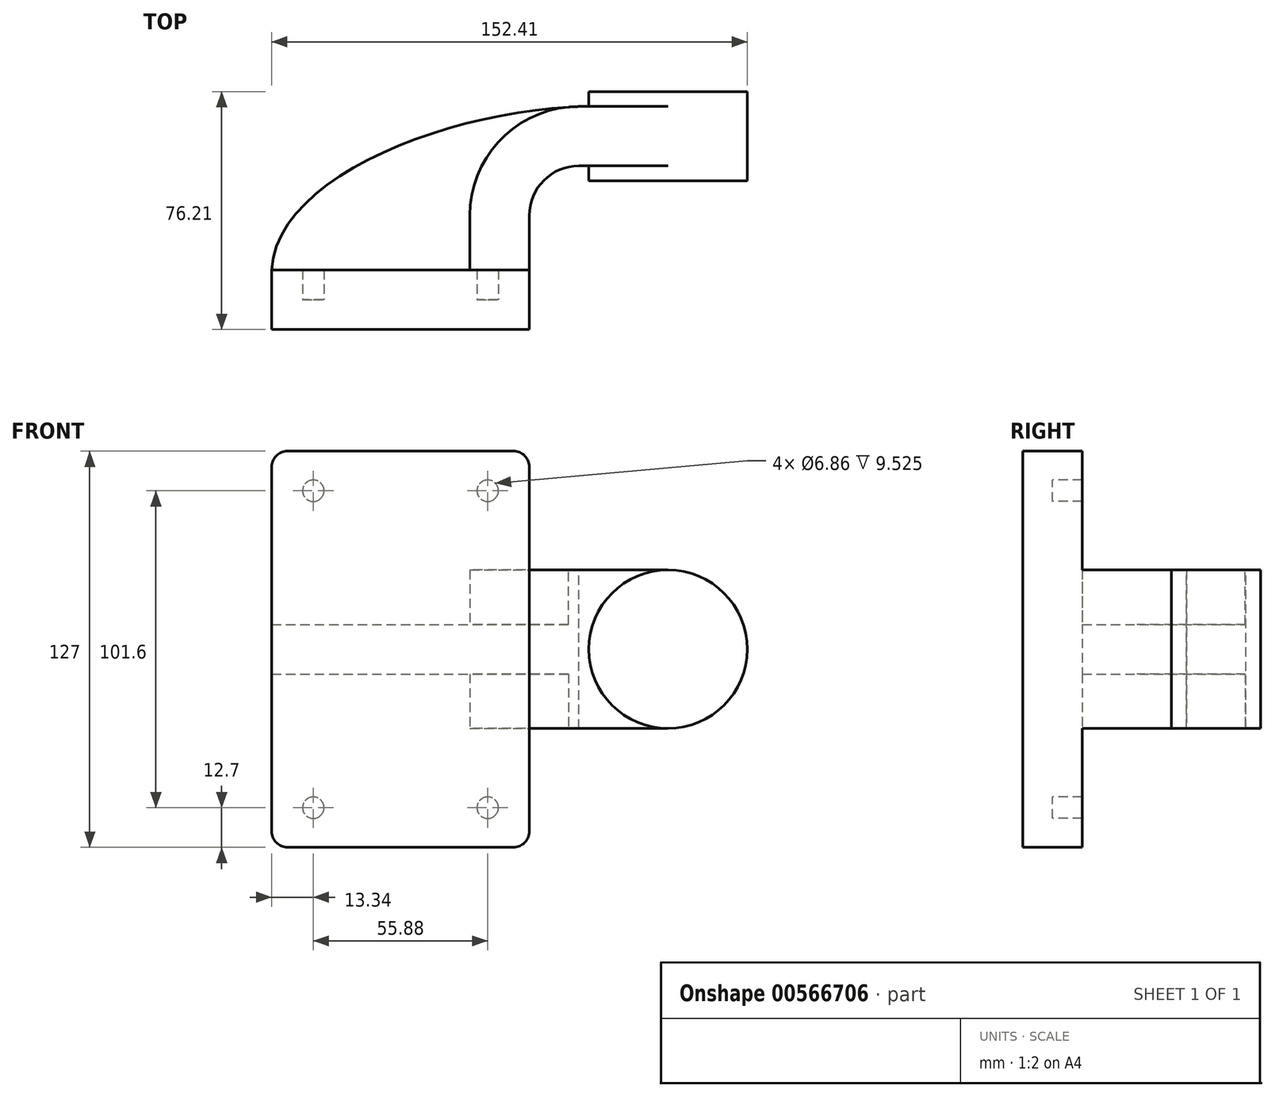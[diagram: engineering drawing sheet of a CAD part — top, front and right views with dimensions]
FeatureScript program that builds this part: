
annotation { "Feature Type Name" : "Feature", "Feature Type Description" : "" }
export const myFeature = defineFeature(function(context is Context, id is Id, definition is map)
    precondition{}
    {
        {
            var Q0;
            Q0=qCreatedBy(makeId("Top.planeOp"),FACE);
            var sketch = newSketch(context, id + "F0", { "sketchPlane" : qUnion([Q0])});
            skLineSegment(sketch, "E0.rect.bottom", {"start": v(-41.28, 9.52) * mm, "end": v(41.28, 9.52) * mm});
            skLineSegment(sketch, "E0.rect.top", {"start": v(-41.28, -9.52) * mm, "end": v(41.28, -9.52) * mm});
            skLineSegment(sketch, "E0.rect.left", {"start": v(-41.28, 9.52) * mm, "end": v(-41.28, -9.52) * mm});
            skLineSegment(sketch, "E0.rect.right", {"start": v(41.28, 9.52) * mm, "end": v(41.28, -9.52) * mm});
            skPoint(sketch, "E0.rect.middle", {"position": v(0, 0) * mm});
            skLineSegment(sketch, "E1", {"start": v(41.28, 9.52) * mm, "end": v(41.28, 27) * mm});
            skArc(sketch, "E2", {"start": v(41.28, 27) * mm, "mid": v(45.92, 38.23) * mm, "end": v(57.15, 42.88) * mm});
            skLineSegment(sketch, "E3", {"start": v(57.15, 42.88) * mm, "end": v(85.72, 42.88) * mm});
            skLineSegment(sketch, "E4.rect.bottom", {"start": v(60.32, 38.1) * mm, "end": v(111.12, 38.1) * mm});
            skLineSegment(sketch, "E4.rect.top", {"start": v(60.32, 66.68) * mm, "end": v(111.12, 66.68) * mm});
            skLineSegment(sketch, "E4.rect.left", {"start": v(60.32, 38.1) * mm, "end": v(60.32, 66.68) * mm});
            skLineSegment(sketch, "E4.rect.right", {"start": v(111.13, 38.1) * mm, "end": v(111.12, 66.68) * mm});
            skPoint(sketch, "E4.rect.middle", {"position": v(85.72, 52.39) * mm});
            skLineSegment(sketch, "E5.0", {"start": v(57.15, 61.93) * mm, "end": v(85.72, 61.93) * mm});
            skArc(sketch, "E5.1", {"start": v(22.23, 27) * mm, "mid": v(32.45, 51.7) * mm, "end": v(57.15, 61.93) * mm});
            skLineSegment(sketch, "E5.2", {"start": v(22.23, 9.52) * mm, "end": v(22.23, 27) * mm});
            skLineSegment(sketch, "E6", {"start": v(85.72, 38.1) * mm, "end": v(85.72, 66.68) * mm});
            skFitSpline(sketch, "E7", {"points": [v(-41.28, 9.53) * mm, v(57.15, 61.93) * mm], "startDerivative": vector(5.2, 92.34) * mm, "endDerivative": vector(120.92, 4.22) * mm});
            skSolve(sketch);
        }
        {
            var Q0;
            Q0=makeQuery(id+"F0.imprint","IMPRINT",FACE,{"disambiguationData":[TD([[makeQuery(id+"F0.imprint","IMPRINT",EDGE,{"derivedFrom":sQuery(id+"F0.wireOp",EDGE,"E0.rect.top")}),1.0]])]});
            extrude(context, id + "F1", {"entities" : qUnion([Q0]), "endBound" : BoundingType.SYMMETRIC, "depth" : 127 * mm, "offsetDistance" : 25.4 * mm});
        }
        {
            var Q0;
            {var subQ9=sQuery(id+"F0.wireOp",EDGE,"E1");Q0=makeQuery(id+"F0.imprint","IMPRINT",FACE,{"disambiguationData":[TD([[makeQuery(id+"F0.imprint","IMPRINT",EDGE,{"derivedFrom":subQ9}),1.0]])]});}
            var Q1;
            {var subQ0=sQuery(id+"F0.wireOp",EDGE,"E6");var subQ1=sQuery(id+"F0.wireOp",EDGE,"E3");var subQ2=makeQuery(id+"F0.imprint","INTERSECT",VERTEX,{"derivedFrom":[subQ1,subQ0]});Q1=makeQuery(id+"F0.imprint","IMPRINT",FACE,{"disambiguationData":[TD([[makeQuery(id+"F0.imprint","IMPRINT",EDGE,{"disambiguationData":[TD([[subQ2,1.0]])],"derivedFrom":subQ1}),1.0]])]});}
            extrude(context, id + "F2", {"entities" : qUnion([Q0, Q1]), "operationType" : NewBodyOperationType.ADD, "endBound" : BoundingType.SYMMETRIC, "depth" : 50.8 * mm});
        }
        {
            var Q0;
            {var subQ3=sQuery(id+"F0.wireOp",EDGE,"E5.2");Q0=makeQuery(id+"F0.imprint","IMPRINT",FACE,{"disambiguationData":[TD([[makeQuery(id+"F0.imprint","IMPRINT",EDGE,{"derivedFrom":subQ3}),1.0]])]});}
            extrude(context, id + "F3", {"entities" : qUnion([Q0]), "operationType" : NewBodyOperationType.ADD, "endBound" : BoundingType.SYMMETRIC, "depth" : 15.88 * mm});
        }
        {
            var Q0;
            {var subQ5=sQuery(id+"F0.wireOp",EDGE,"E4.rect.right");Q0=makeQuery(id+"F0.imprint","IMPRINT",FACE,{"disambiguationData":[TD([[makeQuery(id+"F0.imprint","IMPRINT",EDGE,{"derivedFrom":subQ5}),1.0]])]});}
            var Q1;
            Q1=sQuery(id+"F0.wireOp",EDGE,"E6");
            revolve(context, id + "F4", {"operationType" : NewBodyOperationType.ADD, "entities" : qUnion([Q0]), "axis" : qUnion([Q1]), "revolveType" : RevolveType.FULL});
        }
        {
            var Q0;
            Q0=makeQuery(id+"F1.opExtrude","CAP_EDGE",EDGE,{"disambiguationData":[OSD([sQuery(id+"F0.wireOp",EDGE,"E0.rect.right")])],"isStart":false});
            var Q1;
            Q1=makeQuery(id+"F1.opExtrude","CAP_EDGE",EDGE,{"disambiguationData":[OSD([sQuery(id+"F0.wireOp",EDGE,"E0.rect.left")])],"isStart":false});
            var Q2;
            Q2=makeQuery(id+"F1.opExtrude","CAP_EDGE",EDGE,{"disambiguationData":[OSD([sQuery(id+"F0.wireOp",EDGE,"E0.rect.right")])],"isStart":true});
            var Q3;
            Q3=makeQuery(id+"F1.opExtrude","CAP_EDGE",EDGE,{"disambiguationData":[OSD([sQuery(id+"F0.wireOp",EDGE,"E0.rect.left")])],"isStart":true});
            fillet(context, id + "F5", {"entities" : qUnion([Q0, Q1, Q2, Q3]), "radius" : 5.08 * mm, "tangentPropagation" : true, "allowEdgeOverflow" : false});
        }
        {
            var Q0;
            Q0=qCreatedBy(makeId("Front.planeOp"),FACE);
            var sketch = newSketch(context, id + "F6", { "sketchPlane" : qUnion([Q0])});
            skLineSegment(sketch, "E8.bottom", {"start": v(-27.94, 50.8) * mm, "end": v(27.94, 50.8) * mm});
            skLineSegment(sketch, "E8.top", {"start": v(-27.94, -50.8) * mm, "end": v(27.94, -50.8) * mm});
            skLineSegment(sketch, "E8.left", {"start": v(-27.94, 50.8) * mm, "end": v(-27.94, -50.8) * mm});
            skLineSegment(sketch, "E8.right", {"start": v(27.94, 50.8) * mm, "end": v(27.94, -50.8) * mm});
            skPoint(sketch, "E8.middle", {"position": v(0, 0) * mm});
            skSolve(sketch);
        }
        {
            var Q0;
            Q0=sQuery(id+"F6.wireOp",VERTEX,"E8.bottom.start");
            var Q1;
            Q1=makeQuery(id+"F1.opExtrude","SWEPT_BODY",BODY,{"disambiguationData":[OSD([sQuery(id+"F0.wireOp",EDGE,"E0.rect.bottom"),sQuery(id+"F0.wireOp",EDGE,"E0.rect.top"),sQuery(id+"F0.wireOp",EDGE,"E0.rect.left"),sQuery(id+"F0.wireOp",EDGE,"E0.rect.right")])]});
            hole(context, id + "F7", {"style" : HoleStyle.SIMPLE, "endStyle" : HoleEndStyle.THROUGH, "holeDiameter" : 6.86 * mm, "isTappedThrough" : true, "tappedDepth" : 12.7 * mm, "tapClearance" : 3, "locations" : qUnion([Q0]), "scope" : qUnion([Q1])});
        }
        {
            var Q0;
            Q0=sQuery(id+"F6.wireOp",VERTEX,"E8.right.start");
            var Q1;
            Q1=makeQuery(id+"F1.opExtrude","SWEPT_BODY",BODY,{"disambiguationData":[OSD([sQuery(id+"F0.wireOp",EDGE,"E0.rect.bottom"),sQuery(id+"F0.wireOp",EDGE,"E0.rect.top"),sQuery(id+"F0.wireOp",EDGE,"E0.rect.left"),sQuery(id+"F0.wireOp",EDGE,"E0.rect.right")])]});
            hole(context, id + "F8", {"style" : HoleStyle.SIMPLE, "endStyle" : HoleEndStyle.THROUGH, "holeDiameter" : 6.86 * mm, "isTappedThrough" : true, "tappedDepth" : 12.7 * mm, "tapClearance" : 3, "locations" : qUnion([Q0]), "scope" : qUnion([Q1])});
        }
        {
            var Q0;
            Q0=sQuery(id+"F6.wireOp",VERTEX,"E8.right.end");
            var Q1;
            Q1=makeQuery(id+"F1.opExtrude","SWEPT_BODY",BODY,{"disambiguationData":[OSD([sQuery(id+"F0.wireOp",EDGE,"E0.rect.bottom"),sQuery(id+"F0.wireOp",EDGE,"E0.rect.top"),sQuery(id+"F0.wireOp",EDGE,"E0.rect.left"),sQuery(id+"F0.wireOp",EDGE,"E0.rect.right")])]});
            hole(context, id + "F9", {"style" : HoleStyle.SIMPLE, "endStyle" : HoleEndStyle.THROUGH, "holeDiameter" : 6.86 * mm, "isTappedThrough" : true, "tappedDepth" : 12.7 * mm, "tapClearance" : 3, "locations" : qUnion([Q0]), "scope" : qUnion([Q1])});
        }
        {
            var Q0;
            Q0=sQuery(id+"F6.wireOp",VERTEX,"E8.left.end");
            var Q1;
            Q1=makeQuery(id+"F1.opExtrude","SWEPT_BODY",BODY,{"disambiguationData":[OSD([sQuery(id+"F0.wireOp",EDGE,"E0.rect.bottom"),sQuery(id+"F0.wireOp",EDGE,"E0.rect.top"),sQuery(id+"F0.wireOp",EDGE,"E0.rect.left"),sQuery(id+"F0.wireOp",EDGE,"E0.rect.right")])]});
            hole(context, id + "F10", {"style" : HoleStyle.SIMPLE, "endStyle" : HoleEndStyle.THROUGH, "holeDiameter" : 6.86 * mm, "isTappedThrough" : true, "tappedDepth" : 12.7 * mm, "tapClearance" : 3, "locations" : qUnion([Q0]), "scope" : qUnion([Q1])});
        }
    });
